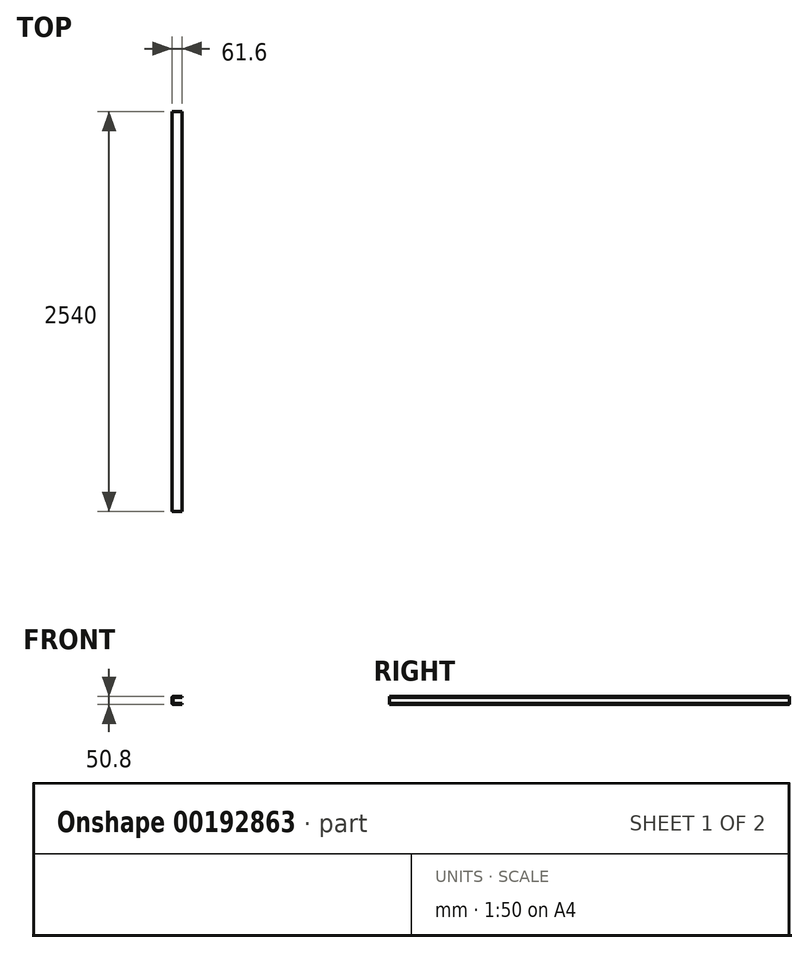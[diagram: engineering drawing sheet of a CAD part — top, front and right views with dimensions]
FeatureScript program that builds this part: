
annotation { "Feature Type Name" : "Feature", "Feature Type Description" : "" }
export const myFeature = defineFeature(function(context is Context, id is Id, definition is map)
    precondition{}
    {
        {
            var Q0;
            Q0=qCreatedBy(makeId("Front.planeOp"),FACE);
            var sketch = newSketch(context, id + "F0", { "sketchPlane" : qUnion([Q0])});
            skLineSegment(sketch, "E0", {"start": v(0, 0) * mm, "end": v(-53.98, 0) * mm});
            skLineSegment(sketch, "E1", {"start": v(-61.6, 7.62) * mm, "end": v(-61.6, 43.18) * mm});
            skLineSegment(sketch, "E2", {"start": v(-53.98, 50.8) * mm, "end": v(0, 50.8) * mm});
            skPoint(sketch, "E3.visualSharp", {"position": v(-61.6, 50.8) * mm});
            skArc(sketch, "E3.filletArc", {"start": v(-53.98, 50.8) * mm, "mid": v(-59.37, 48.57) * mm, "end": v(-61.6, 43.18) * mm});
            skPoint(sketch, "E4.visualSharp", {"position": v(-61.6, 0) * mm});
            skArc(sketch, "E4.filletArc", {"start": v(-61.6, 7.62) * mm, "mid": v(-59.37, 2.23) * mm, "end": v(-53.98, 0) * mm});
            skLineSegment(sketch, "E5.0", {"start": v(-53.98, 44.45) * mm, "end": v(0, 44.45) * mm});
            skLineSegment(sketch, "E6.0", {"start": v(-55.25, 7.62) * mm, "end": v(-55.25, 43.18) * mm});
            skLineSegment(sketch, "E7.0", {"start": v(0, 6.35) * mm, "end": v(-53.98, 6.35) * mm});
            skPoint(sketch, "E8.visualSharp", {"position": v(-55.25, 44.45) * mm});
            skArc(sketch, "E8.filletArc", {"start": v(-53.98, 44.45) * mm, "mid": v(-54.87, 44.08) * mm, "end": v(-55.25, 43.18) * mm});
            skPoint(sketch, "E9.visualSharp", {"position": v(-55.25, 6.35) * mm});
            skArc(sketch, "E9.filletArc", {"start": v(-55.25, 7.62) * mm, "mid": v(-54.87, 6.72) * mm, "end": v(-53.98, 6.35) * mm});
            skLineSegment(sketch, "E10", {"start": v(0, 50.8) * mm, "end": v(0, 44.45) * mm});
            skLineSegment(sketch, "E11", {"start": v(0, 6.35) * mm, "end": v(0, 0) * mm});
            skSolve(sketch);
        }
        {
            var Q0;
            Q0 = qSketchRegion(id + "F0", true);
            extrude(context, id + "F1", {"entities" : qUnion([Q0]), "depth" : 2540 * mm});
        }
    });
